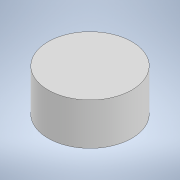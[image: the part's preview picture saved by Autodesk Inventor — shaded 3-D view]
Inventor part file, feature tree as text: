
AUTODESK INVENTOR PART (.ipt)
format: ipt  version: 2020.3 (Build 243373000, 373)  size: 87,552 bytes
history: native  units: in
note: dims shown in document units (in); Inventor stores cm internally (conversion verified against a paired STEP export)
features: extrude x1, sketch x1
ambient origin geometry x8: Origin, YZ Plane, XZ Plane, XY Plane, X Axis, Y Axis, Z Axis, Center Point
bodies: Solid1 (feature_tree)
feature tree (2):
  extrude  "Extrusion1"  Depth=0.5in TaperAngle=0.0deg
  sketch  "Sketch1"  dims[d0=1.0in d1=0.5in d2=0.0in]
